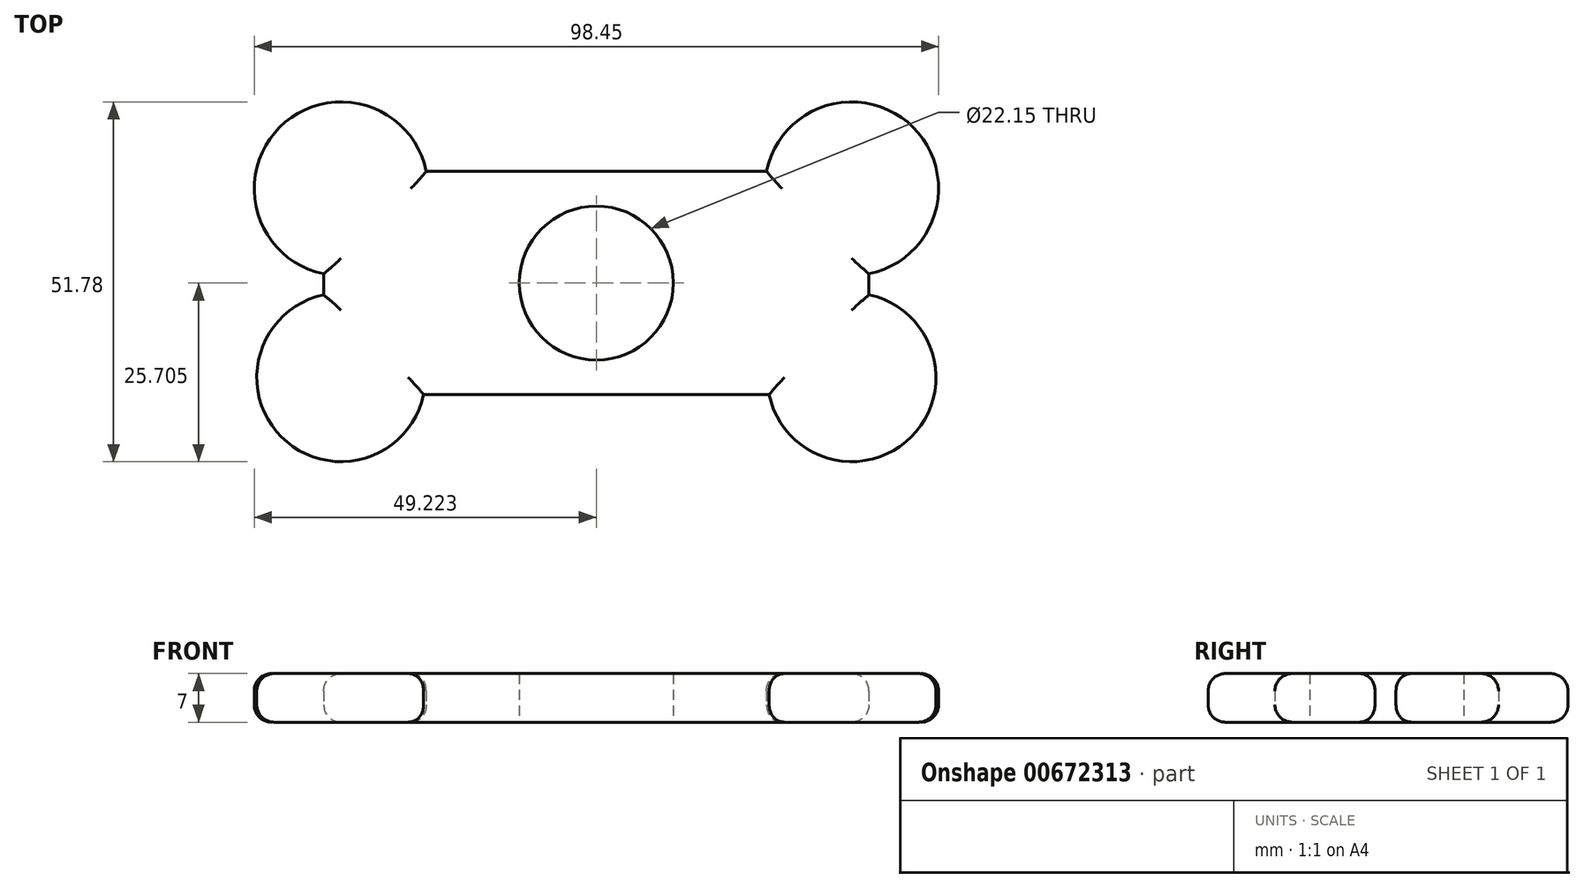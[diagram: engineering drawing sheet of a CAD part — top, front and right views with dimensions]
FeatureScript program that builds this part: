
annotation { "Feature Type Name" : "Feature", "Feature Type Description" : "" }
export const myFeature = defineFeature(function(context is Context, id is Id, definition is map)
    precondition{}
    {
        {
            var Q0;
            Q0=qCreatedBy(makeId("Top.planeOp"),FACE);
            var sketch = newSketch(context, id + "F0", { "sketchPlane" : qUnion([Q0])});
            skCircle(sketch, "E0", {"center": v(0.22, -0.02) * mm, "radius": 11.07 * mm});
            skLineSegment(sketch, "E1.bottom", {"start": v(39.45, -16.1) * mm, "end": v(-39, -16.1) * mm});
            skLineSegment(sketch, "E1.top", {"start": v(39.45, 16.05) * mm, "end": v(-39, 16.05) * mm});
            skLineSegment(sketch, "E1.left", {"start": v(39.45, -16.1) * mm, "end": v(39.45, 16.05) * mm});
            skLineSegment(sketch, "E1.right", {"start": v(-39, -16.1) * mm, "end": v(-39, 16.05) * mm});
            skPoint(sketch, "E1.middle", {"position": v(-1.78, -0.02) * mm});
            skCircle(sketch, "E2", {"center": v(36.95, 13.55) * mm, "radius": 12.5 * mm});
            skCircle(sketch, "E3", {"center": v(36.95, -13.6) * mm, "radius": 12.13 * mm});
            skCircle(sketch, "E4", {"center": v(-36.5, 13.55) * mm, "radius": 12.5 * mm});
            skCircle(sketch, "E5", {"center": v(-36.5, -13.6) * mm, "radius": 12.13 * mm});
            skSolve(sketch);
        }
        {
            var Q0;
            {var subQ0=sQuery(id+"F0.wireOp",EDGE,"E1.right");var subQ1=sQuery(id+"F0.wireOp",EDGE,"E1.top");var subQ2=makeQuery(id+"F0.imprint","INTERSECT",VERTEX,{"derivedFrom":[subQ1,subQ0]});Q0=makeQuery(id+"F0.imprint","IMPRINT",FACE,{"disambiguationData":[TD([[makeQuery(id+"F0.imprint","IMPRINT",EDGE,{"disambiguationData":[TD([[subQ2,1.0]])],"derivedFrom":subQ1}),-1.0]])]});}
            var Q1;
            {var subQ0=sQuery(id+"F0.wireOp",EDGE,"E1.right");var subQ1=sQuery(id+"F0.wireOp",EDGE,"E1.top");var subQ2=makeQuery(id+"F0.imprint","INTERSECT",VERTEX,{"derivedFrom":[subQ1,subQ0]});Q1=makeQuery(id+"F0.imprint","IMPRINT",FACE,{"disambiguationData":[TD([[makeQuery(id+"F0.imprint","IMPRINT",EDGE,{"disambiguationData":[TD([[subQ2,1.0]])],"derivedFrom":subQ1}),1.0]])]});}
            var Q2;
            Q2=makeQuery(id+"F0.imprint","IMPRINT",FACE,{"disambiguationData":[TD([[makeQuery(id+"F0.imprint","IMPRINT",EDGE,{"derivedFrom":sQuery(id+"F0.wireOp",EDGE,"E0")}),-1.0]])]});
            var Q3;
            {var subQ0=sQuery(id+"F0.wireOp",EDGE,"E1.left");var subQ1=sQuery(id+"F0.wireOp",EDGE,"E1.top");var subQ2=makeQuery(id+"F0.imprint","INTERSECT",VERTEX,{"derivedFrom":[subQ1,subQ0]});Q3=makeQuery(id+"F0.imprint","IMPRINT",FACE,{"disambiguationData":[TD([[makeQuery(id+"F0.imprint","IMPRINT",EDGE,{"disambiguationData":[TD([[subQ2,-1.0]])],"derivedFrom":subQ1}),1.0]])]});}
            var Q4;
            {var subQ0=sQuery(id+"F0.wireOp",EDGE,"E1.left");var subQ1=sQuery(id+"F0.wireOp",EDGE,"E1.bottom");var subQ2=makeQuery(id+"F0.imprint","INTERSECT",VERTEX,{"derivedFrom":[subQ1,subQ0]});Q4=makeQuery(id+"F0.imprint","IMPRINT",FACE,{"disambiguationData":[TD([[makeQuery(id+"F0.imprint","IMPRINT",EDGE,{"disambiguationData":[TD([[subQ2,-1.0]])],"derivedFrom":subQ1}),-1.0]])]});}
            var Q5;
            {var subQ0=sQuery(id+"F0.wireOp",EDGE,"E1.left");var subQ1=sQuery(id+"F0.wireOp",EDGE,"E1.top");var subQ2=makeQuery(id+"F0.imprint","INTERSECT",VERTEX,{"derivedFrom":[subQ1,subQ0]});Q5=makeQuery(id+"F0.imprint","IMPRINT",FACE,{"disambiguationData":[TD([[makeQuery(id+"F0.imprint","IMPRINT",EDGE,{"disambiguationData":[TD([[subQ2,-1.0]])],"derivedFrom":subQ1}),-1.0]])]});}
            var Q6;
            {var subQ0=sQuery(id+"F0.wireOp",EDGE,"E1.left");var subQ1=sQuery(id+"F0.wireOp",EDGE,"E1.bottom");var subQ2=makeQuery(id+"F0.imprint","INTERSECT",VERTEX,{"derivedFrom":[subQ1,subQ0]});Q6=makeQuery(id+"F0.imprint","IMPRINT",FACE,{"disambiguationData":[TD([[makeQuery(id+"F0.imprint","IMPRINT",EDGE,{"disambiguationData":[TD([[subQ2,-1.0]])],"derivedFrom":subQ1}),1.0]])]});}
            var Q7;
            {var subQ0=sQuery(id+"F0.wireOp",EDGE,"E1.right");var subQ1=sQuery(id+"F0.wireOp",EDGE,"E1.bottom");var subQ2=makeQuery(id+"F0.imprint","INTERSECT",VERTEX,{"derivedFrom":[subQ1,subQ0]});Q7=makeQuery(id+"F0.imprint","IMPRINT",FACE,{"disambiguationData":[TD([[makeQuery(id+"F0.imprint","IMPRINT",EDGE,{"disambiguationData":[TD([[subQ2,1.0]])],"derivedFrom":subQ1}),1.0]])]});}
            var Q8;
            {var subQ0=sQuery(id+"F0.wireOp",EDGE,"E1.right");var subQ1=sQuery(id+"F0.wireOp",EDGE,"E1.bottom");var subQ2=makeQuery(id+"F0.imprint","INTERSECT",VERTEX,{"derivedFrom":[subQ1,subQ0]});Q8=makeQuery(id+"F0.imprint","IMPRINT",FACE,{"disambiguationData":[TD([[makeQuery(id+"F0.imprint","IMPRINT",EDGE,{"disambiguationData":[TD([[subQ2,1.0]])],"derivedFrom":subQ1}),-1.0]])]});}
            extrude(context, id + "F1", {"entities" : qUnion([Q0, Q1, Q2, Q3, Q4, Q5, Q6, Q7, Q8]), "depth" : 7 * mm, "offsetDistance" : 25 * mm});
        }
        {
            var Q0;
            Q0=makeQuery(id+"F1.opExtrude","CAP_EDGE",EDGE,{"disambiguationData":[OSD([sQuery(id+"F0.wireOp",EDGE,"E4")])],"isStart":false});
            var Q1;
            Q1=makeQuery(id+"F1.opExtrude","CAP_EDGE",EDGE,{"disambiguationData":[OSD([sQuery(id+"F0.wireOp",EDGE,"E1.top")])],"isStart":false});
            var Q2;
            Q2=makeQuery(id+"F1.opExtrude","CAP_EDGE",EDGE,{"disambiguationData":[OSD([sQuery(id+"F0.wireOp",EDGE,"E2")])],"isStart":false});
            var Q3;
            Q3=makeQuery(id+"F1.opExtrude","CAP_EDGE",EDGE,{"disambiguationData":[OSD([sQuery(id+"F0.wireOp",EDGE,"E1.left")])],"isStart":false});
            var Q4;
            Q4=makeQuery(id+"F1.opExtrude","CAP_EDGE",EDGE,{"disambiguationData":[OSD([sQuery(id+"F0.wireOp",EDGE,"E3")])],"isStart":false});
            var Q5;
            Q5=makeQuery(id+"F1.opExtrude","CAP_EDGE",EDGE,{"disambiguationData":[OSD([sQuery(id+"F0.wireOp",EDGE,"E1.bottom")])],"isStart":false});
            var Q6;
            Q6=makeQuery(id+"F1.opExtrude","CAP_EDGE",EDGE,{"disambiguationData":[OSD([sQuery(id+"F0.wireOp",EDGE,"E5")])],"isStart":false});
            var Q7;
            Q7=makeQuery(id+"F1.opExtrude","CAP_EDGE",EDGE,{"disambiguationData":[OSD([sQuery(id+"F0.wireOp",EDGE,"E1.right")])],"isStart":false});
            var Q8;
            Q8=makeQuery(id+"F1.opExtrude","CAP_EDGE",EDGE,{"disambiguationData":[OSD([sQuery(id+"F0.wireOp",EDGE,"E5")])],"isStart":true});
            var Q9;
            Q9=makeQuery(id+"F1.opExtrude","CAP_EDGE",EDGE,{"disambiguationData":[OSD([sQuery(id+"F0.wireOp",EDGE,"E1.bottom")])],"isStart":true});
            var Q10;
            Q10=makeQuery(id+"F1.opExtrude","CAP_EDGE",EDGE,{"disambiguationData":[OSD([sQuery(id+"F0.wireOp",EDGE,"E3")])],"isStart":true});
            var Q11;
            Q11=makeQuery(id+"F1.opExtrude","CAP_EDGE",EDGE,{"disambiguationData":[OSD([sQuery(id+"F0.wireOp",EDGE,"E1.left")])],"isStart":true});
            var Q12;
            Q12=makeQuery(id+"F1.opExtrude","CAP_EDGE",EDGE,{"disambiguationData":[OSD([sQuery(id+"F0.wireOp",EDGE,"E2")])],"isStart":true});
            var Q13;
            Q13=makeQuery(id+"F1.opExtrude","CAP_EDGE",EDGE,{"disambiguationData":[OSD([sQuery(id+"F0.wireOp",EDGE,"E1.top")])],"isStart":true});
            var Q14;
            Q14=makeQuery(id+"F1.opExtrude","CAP_EDGE",EDGE,{"disambiguationData":[OSD([sQuery(id+"F0.wireOp",EDGE,"E4")])],"isStart":true});
            var Q15;
            Q15=makeQuery(id+"F1.opExtrude","CAP_EDGE",EDGE,{"disambiguationData":[OSD([sQuery(id+"F0.wireOp",EDGE,"E1.right")])],"isStart":true});
            fillet(context, id + "F2", {"entities" : qUnion([Q0, Q1, Q2, Q3, Q4, Q5, Q6, Q7, Q8, Q9, Q10, Q11, Q12, Q13, Q14, Q15]), "radius" : 2.5 * mm, "tangentPropagation" : true, "allowEdgeOverflow" : false});
        }
    });
